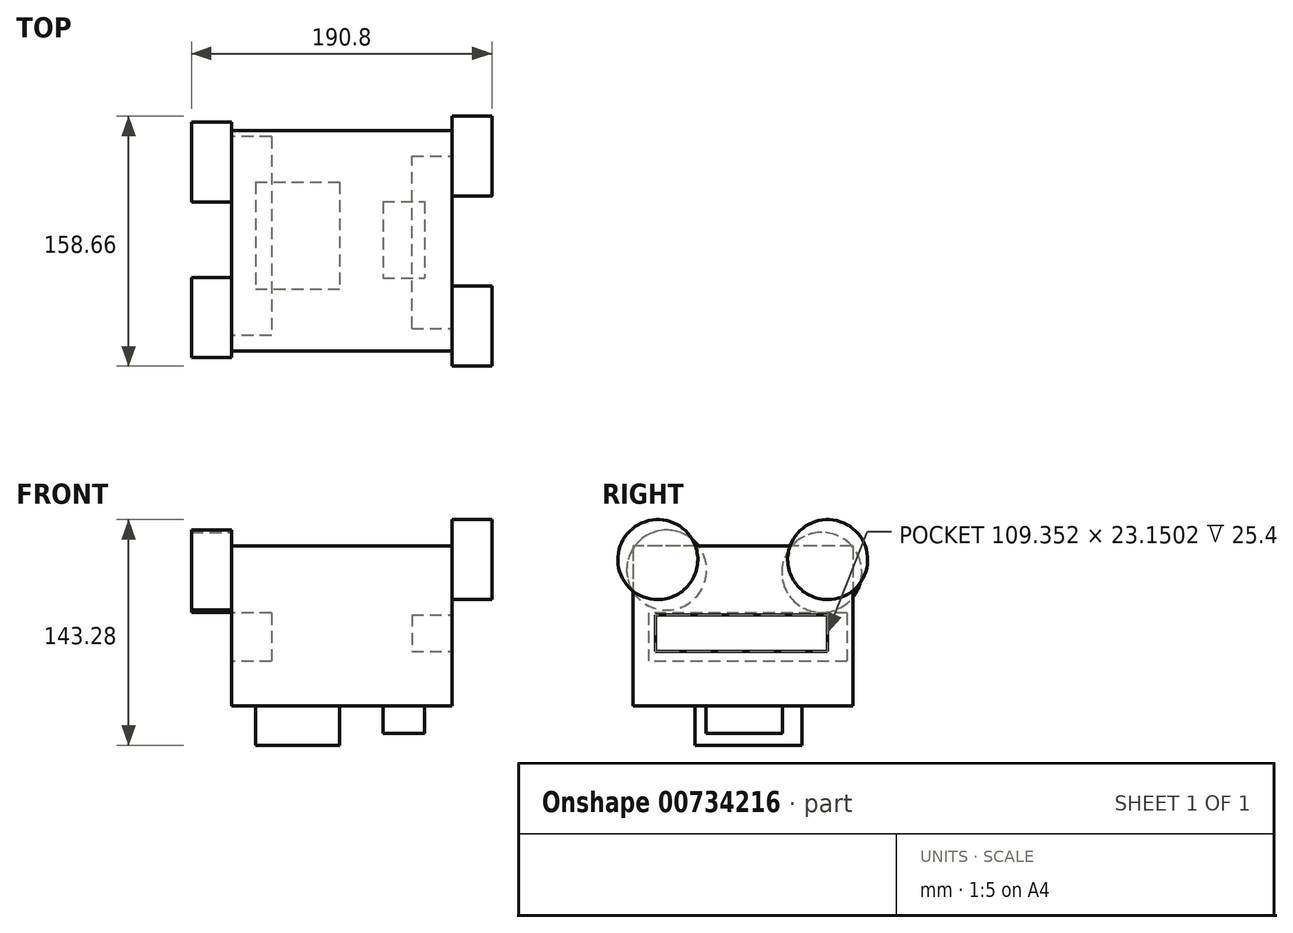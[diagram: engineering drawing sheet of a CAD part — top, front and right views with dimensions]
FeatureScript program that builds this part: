
annotation { "Feature Type Name" : "Feature", "Feature Type Description" : "" }
export const myFeature = defineFeature(function(context is Context, id is Id, definition is map)
    precondition{}
    {
        {
            var Q0;
            Q0=qCreatedBy(makeId("Top.planeOp"),FACE);
            var sketch = newSketch(context, id + "F0", { "sketchPlane" : qUnion([Q0])});
            skLineSegment(sketch, "E0.bottom", {"start": v(70, 70) * mm, "end": v(-70, 70) * mm});
            skLineSegment(sketch, "E0.top", {"start": v(70, -70) * mm, "end": v(-70, -70) * mm});
            skLineSegment(sketch, "E0.left", {"start": v(70, 70) * mm, "end": v(70, -70) * mm});
            skLineSegment(sketch, "E0.right", {"start": v(-70, 70) * mm, "end": v(-70, -70) * mm});
            skPoint(sketch, "E0.middle", {"position": v(0, 0) * mm});
            skSolve(sketch);
        }
        {
            var Q0;
            Q0=makeQuery(id+"F0.imprint","IMPRINT",FACE,{"disambiguationData":[TD([[makeQuery(id+"F0.imprint","IMPRINT",EDGE,{"derivedFrom":sQuery(id+"F0.wireOp",EDGE,"E0.bottom")}),1.0]])]});
            extrude(context, id + "F1", {"entities" : qUnion([Q0]), "depth" : 101.6 * mm, "offsetDistance" : 25.4 * mm});
        }
        {
            var Q0;
            Q0=makeQuery(id+"F0.imprint","IMPRINT",FACE,{"disambiguationData":[TD([[makeQuery(id+"F0.imprint","IMPRINT",EDGE,{"derivedFrom":sQuery(id+"F0.wireOp",EDGE,"E0.bottom")}),1.0]])]});
            var sketch = newSketch(context, id + "F2", { "sketchPlane" : qUnion([Q0])});
            skLineSegment(sketch, "E1.bottom", {"start": v(26.2, 25.05) * mm, "end": v(52.7, 25.05) * mm});
            skLineSegment(sketch, "E1.top", {"start": v(26.2, -23.45) * mm, "end": v(52.7, -23.45) * mm});
            skLineSegment(sketch, "E1.left", {"start": v(26.2, 25.05) * mm, "end": v(26.2, -23.45) * mm});
            skLineSegment(sketch, "E1.right", {"start": v(52.7, 25.05) * mm, "end": v(52.7, -23.45) * mm});
            skSolve(sketch);
        }
        {
            var Q0;
            Q0=makeQuery(id+"F0.imprint","IMPRINT",FACE,{"disambiguationData":[TD([[makeQuery(id+"F0.imprint","IMPRINT",EDGE,{"derivedFrom":sQuery(id+"F0.wireOp",EDGE,"E0.bottom")}),1.0]])]});
            var sketch = newSketch(context, id + "F3", { "sketchPlane" : qUnion([Q0])});
            skLineSegment(sketch, "E2.bottom", {"start": v(-54.72, 37.41) * mm, "end": v(-1.32, 37.41) * mm});
            skLineSegment(sketch, "E2.top", {"start": v(-54.72, -30.59) * mm, "end": v(-1.32, -30.59) * mm});
            skLineSegment(sketch, "E2.left", {"start": v(-54.72, 37.41) * mm, "end": v(-54.72, -30.59) * mm});
            skLineSegment(sketch, "E2.right", {"start": v(-1.32, 37.41) * mm, "end": v(-1.32, -30.59) * mm});
            skSolve(sketch);
        }
        {
            var Q0;
            Q0 = qSketchRegion(id + "F2", true);
            extrude(context, id + "F4", {"entities" : qUnion([Q0]), "oppositeDirection" : true, "depth" : 17.5 * mm, "offsetDistance" : 25.4 * mm});
        }
        {
            var Q0;
            Q0 = qSketchRegion(id + "F3", true);
            extrude(context, id + "F5", {"entities" : qUnion([Q0]), "operationType" : NewBodyOperationType.ADD, "oppositeDirection" : true, "depth" : 25 * mm, "offsetDistance" : 25.4 * mm});
        }
        {
            var Q0;
            Q0=makeQuery(id+"F1.opExtrude","SWEPT_FACE",FACE,{"disambiguationData":[OSD([sQuery(id+"F0.wireOp",EDGE,"E0.left")])]});
            var sketch = newSketch(context, id + "F6", { "sketchPlane" : qUnion([Q0])});
            skLineSegment(sketch, "E3.bottom", {"start": v(-55.56, 57.82) * mm, "end": v(53.79, 57.82) * mm});
            skLineSegment(sketch, "E3.top", {"start": v(-55.56, 34.67) * mm, "end": v(53.79, 34.67) * mm});
            skLineSegment(sketch, "E3.left", {"start": v(-55.56, 57.82) * mm, "end": v(-55.56, 34.67) * mm});
            skLineSegment(sketch, "E3.right", {"start": v(53.79, 57.82) * mm, "end": v(53.79, 34.67) * mm});
            skSolve(sketch);
        }
        {
            var Q0;
            Q0=makeQuery(id+"F6.imprint","IMPRINT",FACE,{"disambiguationData":[TD([[makeQuery(id+"F6.imprint","IMPRINT",EDGE,{"derivedFrom":sQuery(id+"F6.wireOp",EDGE,"E3.bottom")}),-1.0]])]});
            extrude(context, id + "F7", {"entities" : qUnion([Q0]), "operationType" : NewBodyOperationType.REMOVE, "oppositeDirection" : true, "depth" : 25.4 * mm, "offsetDistance" : 25.4 * mm});
        }
        {
            var Q0;
            Q0=makeQuery(id+"F1.opExtrude","SWEPT_FACE",FACE,{"disambiguationData":[OSD([sQuery(id+"F0.wireOp",EDGE,"E0.right")])]});
            var sketch = newSketch(context, id + "F8", { "sketchPlane" : qUnion([Q0])});
            skLineSegment(sketch, "E4.bottom", {"start": v(-66.2, 58.95) * mm, "end": v(60.07, 58.95) * mm});
            skLineSegment(sketch, "E4.top", {"start": v(-66.2, 28.06) * mm, "end": v(60.07, 28.06) * mm});
            skLineSegment(sketch, "E4.left", {"start": v(-66.2, 58.95) * mm, "end": v(-66.2, 28.06) * mm});
            skLineSegment(sketch, "E4.right", {"start": v(60.07, 58.95) * mm, "end": v(60.07, 28.06) * mm});
            skSolve(sketch);
        }
        {
            var Q0;
            Q0=makeQuery(id+"F8.imprint","IMPRINT",FACE,{"disambiguationData":[TD([[makeQuery(id+"F8.imprint","IMPRINT",EDGE,{"derivedFrom":sQuery(id+"F8.wireOp",EDGE,"E4.bottom")}),-1.0]])]});
            extrude(context, id + "F9", {"entities" : qUnion([Q0]), "operationType" : NewBodyOperationType.REMOVE, "oppositeDirection" : true, "depth" : 25.4 * mm, "offsetDistance" : 25.4 * mm});
        }
        {
            var Q0;
            Q0=makeQuery(id+"F1.opExtrude","SWEPT_FACE",FACE,{"disambiguationData":[OSD([sQuery(id+"F0.wireOp",EDGE,"E0.left")])]});
            var sketch = newSketch(context, id + "F10", { "sketchPlane" : qUnion([Q0])});
            skCircle(sketch, "E5", {"center": v(-54.07, 92.88) * mm, "radius": 25.4 * mm});
            skCircle(sketch, "E6", {"center": v(53.79, 92.88) * mm, "radius": 25.4 * mm});
            skSolve(sketch);
        }
        {
            var Q0;
            Q0 = qSketchRegion(id + "F10", true);
            extrude(context, id + "F11", {"entities" : qUnion([Q0]), "operationType" : NewBodyOperationType.ADD, "depth" : 25.4 * mm, "offsetDistance" : 25.4 * mm});
        }
        {
            var Q0;
            Q0=makeQuery(id+"F1.opExtrude","SWEPT_FACE",FACE,{"disambiguationData":[OSD([sQuery(id+"F0.wireOp",EDGE,"E0.right")])]});
            var sketch = newSketch(context, id + "F12", { "sketchPlane" : qUnion([Q0])});
            skCircle(sketch, "E7", {"center": v(-50.04, 84.78) * mm, "radius": 25.4 * mm});
            skCircle(sketch, "E8", {"center": v(48.47, 86.2) * mm, "radius": 25.4 * mm});
            skSolve(sketch);
        }
        {
            var Q0;
            Q0 = qSketchRegion(id + "F12", true);
            extrude(context, id + "F13", {"entities" : qUnion([Q0]), "operationType" : NewBodyOperationType.ADD, "depth" : 25.4 * mm, "offsetDistance" : 25.4 * mm});
        }
    });
